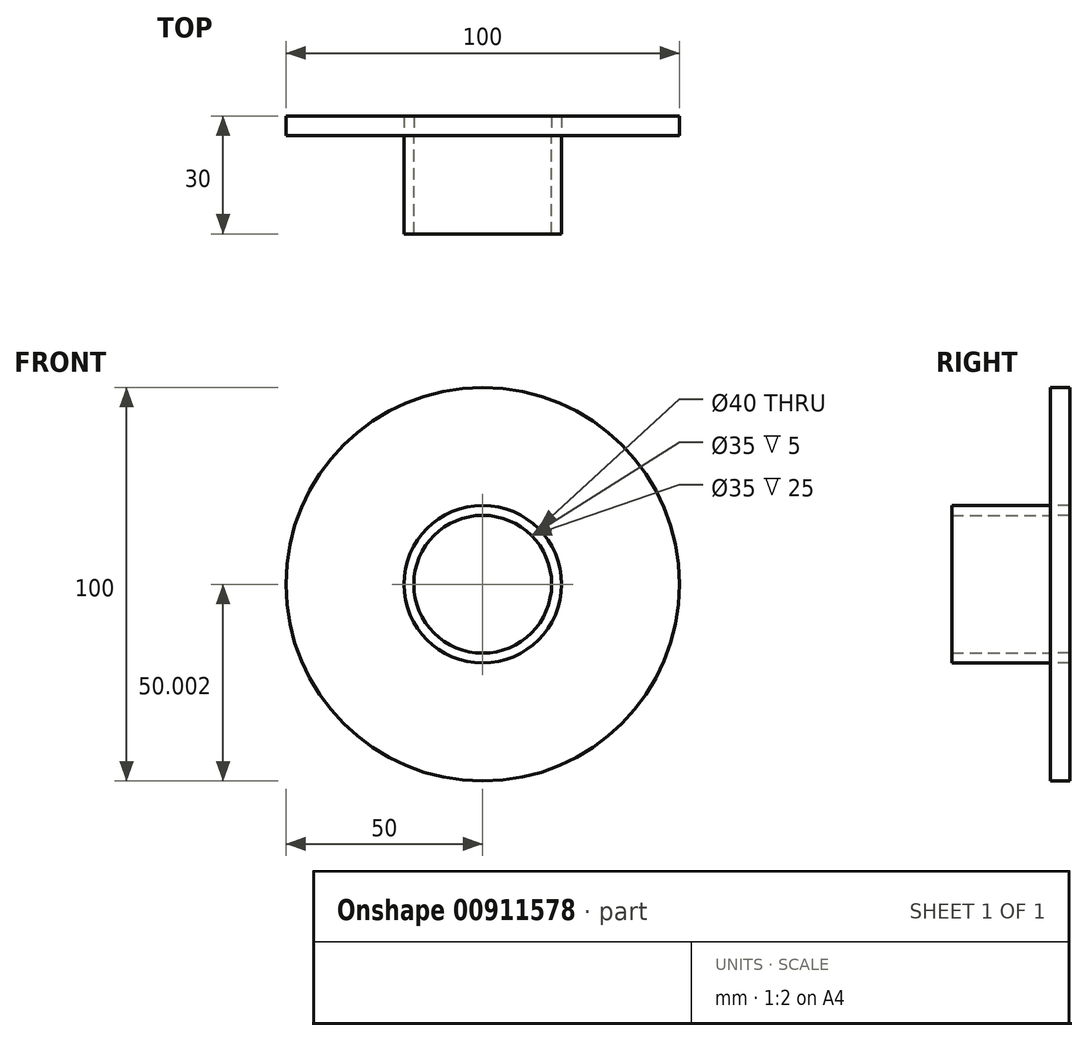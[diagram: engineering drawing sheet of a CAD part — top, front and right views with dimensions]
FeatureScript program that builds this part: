
annotation { "Feature Type Name" : "Feature", "Feature Type Description" : "" }
export const myFeature = defineFeature(function(context is Context, id is Id, definition is map)
    precondition{}
    {
        {
            var Q0;
            Q0=qCreatedBy(makeId("Front.planeOp"),FACE);
            var sketch = newSketch(context, id + "F0", { "sketchPlane" : qUnion([Q0])});
            skCircle(sketch, "E0", {"center": v(0, 92.21) * mm, "radius": 50 * mm});
            skCircle(sketch, "E1", {"center": v(0, 92.21) * mm, "radius": 20 * mm});
            skPoint(sketch, "E2.center.orphan", {"position": v(0, 114.35) * mm});
            skCircle(sketch, "E3", {"center": v(0, 92.21) * mm, "radius": 17.5 * mm});
            skPoint(sketch, "E4.center.orphan", {"position": v(0, -44.74) * mm});
            skSolve(sketch);
        }
        {
            var Q0;
            Q0=makeQuery(id+"F0.imprint","IMPRINT",FACE,{"disambiguationData":[TD([[makeQuery(id+"F0.imprint","IMPRINT",EDGE,{"derivedFrom":sQuery(id+"F0.wireOp",EDGE,"E1")}),1.0]])]});
            extrude(context, id + "F1", {"entities" : qUnion([Q0]), "depth" : 25 * mm, "offsetDistance" : 25 * mm});
        }
        {
            var Q0;
            Q0 = qSketchRegion(id + "F0", true);
            extrude(context, id + "F2", {"entities" : qUnion([Q0]), "oppositeDirection" : true, "depth" : 5 * mm, "offsetDistance" : 25 * mm});
        }
        {
            var Q0;
            Q0=makeQuery(id+"F1.opExtrude","CAP_FACE",FACE,{"disambiguationData":[OSD([sQuery(id+"F0.wireOp",EDGE,"E1"),sQuery(id+"F0.wireOp",EDGE,"E3")])],"isStart":true});
            extrude(context, id + "F3", {"entities" : qUnion([Q0]), "depth" : 5 * mm, "offsetDistance" : 25 * mm});
        }
    });
